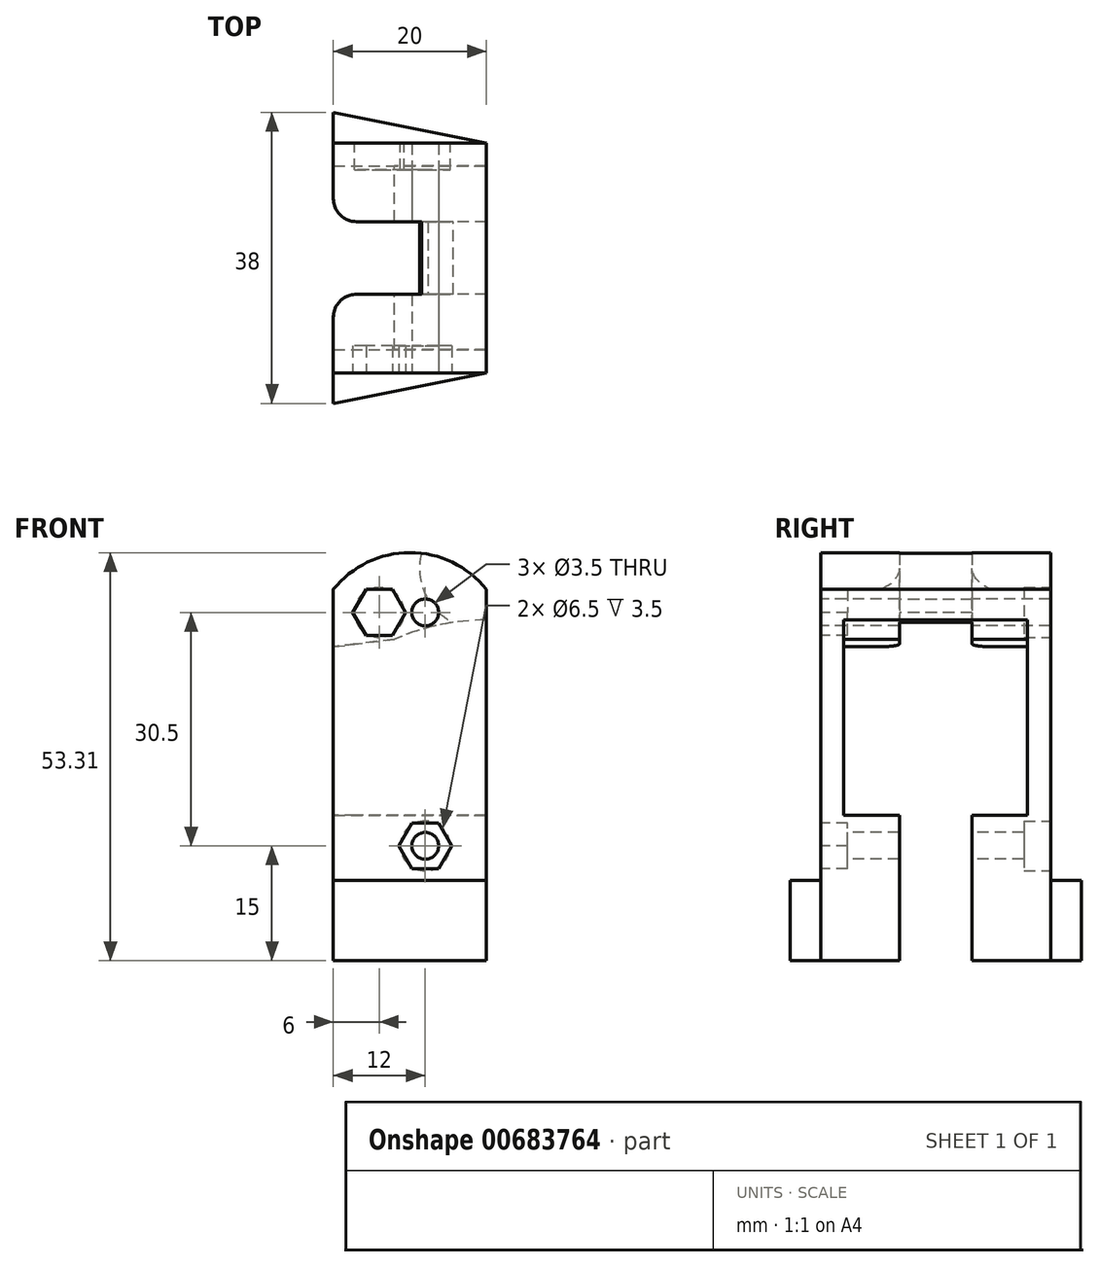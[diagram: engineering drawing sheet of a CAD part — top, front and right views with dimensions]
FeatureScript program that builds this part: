
annotation { "Feature Type Name" : "Feature", "Feature Type Description" : "" }
export const myFeature = defineFeature(function(context is Context, id is Id, definition is map)
    precondition{}
    {
        {
            var Q0;
            Q0=qCreatedBy(makeId("Front.planeOp"),FACE);
            var sketch = newSketch(context, id + "F0", { "sketchPlane" : qUnion([Q0])});
            skLineSegment(sketch, "E0", {"start": v(12, 0) * mm, "end": v(12, 38) * mm});
            skLineSegment(sketch, "E1", {"start": v(12, 0) * mm, "end": v(-8, 0) * mm});
            skLineSegment(sketch, "E2", {"start": v(-8, 0) * mm, "end": v(-8, 38) * mm});
            skArc(sketch, "E3", {"start": v(12, 38) * mm, "mid": v(2, 42.81) * mm, "end": v(-8, 38) * mm});
            skSolve(sketch);
        }
        {
            var Q0;
            Q0=qSketchRegion(id+"F0",true);
            extrude(context, id + "F1", {"entities" : qUnion([Q0]), "endBound" : BoundingType.SYMMETRIC, "depth" : 30 * mm, "offsetDistance" : 25 * mm});
        }
        {
            var Q0;
            Q0=qCreatedBy(makeId("Front.planeOp"),FACE);
            var sketch = newSketch(context, id + "F2", { "sketchPlane" : qUnion([Q0])});
            skLineSegment(sketch, "E4.bottom", {"start": v(12, 0) * mm, "end": v(-8, 0) * mm});
            skLineSegment(sketch, "E4.top", {"start": v(12, -10.5) * mm, "end": v(-8, -10.5) * mm});
            skLineSegment(sketch, "E4.left", {"start": v(12, 0) * mm, "end": v(12, -10.5) * mm});
            skLineSegment(sketch, "E4.right", {"start": v(-8, 0) * mm, "end": v(-8, -10.5) * mm});
            skSolve(sketch);
        }
        {
            var Q0;
            Q0 = qSketchRegion(id + "F2", true);
            extrude(context, id + "F3", {"entities" : qUnion([Q0]), "operationType" : NewBodyOperationType.ADD, "endBound" : BoundingType.SYMMETRIC, "depth" : 38 * mm, "offsetDistance" : 25 * mm});
        }
        {
            var Q0;
            Q0=qCreatedBy(makeId("Front.planeOp"),FACE);
            var sketch = newSketch(context, id + "F4", { "sketchPlane" : qUnion([Q0])});
            skLineSegment(sketch, "E5", {"start": v(12, 33) * mm, "end": v(12, 0) * mm});
            skLineSegment(sketch, "E6", {"start": v(12, 0) * mm, "end": v(-8, 0) * mm});
            skLineSegment(sketch, "E7", {"start": v(-8, 0) * mm, "end": v(-8, 44) * mm});
            skLineSegment(sketch, "E8", {"start": v(-8, 44) * mm, "end": v(4, 44) * mm});
            skArc(sketch, "E9", {"start": v(4, 44) * mm, "mid": v(4.74, 36.13) * mm, "end": v(12, 33) * mm});
            skLineSegment(sketch, "E10.bottom", {"start": v(-8, 0) * mm, "end": v(12, 0) * mm});
            skLineSegment(sketch, "E10.top", {"start": v(-8, -10.5) * mm, "end": v(12, -10.5) * mm});
            skLineSegment(sketch, "E10.left", {"start": v(-8, 0) * mm, "end": v(-8, -10.5) * mm});
            skLineSegment(sketch, "E10.right", {"start": v(12, 0) * mm, "end": v(12, -10.5) * mm});
            skSolve(sketch);
        }
        {
            var Q0;
            Q0=qSketchRegion(id+"F4",true);
            extrude(context, id + "F5", {"entities" : qUnion([Q0]), "endBound" : BoundingType.SYMMETRIC, "depth" : 9.5 * mm, "offsetDistance" : 25 * mm});
        }
        {
            var Q0;
            Q0=makeQuery(id+"F5.opExtrude","SWEPT_BODY",BODY,{"disambiguationData":[OSD([sQuery(id+"F4.wireOp",EDGE,"E5"),sQuery(id+"F4.wireOp",EDGE,"E6"),sQuery(id+"F4.wireOp",EDGE,"E7"),sQuery(id+"F4.wireOp",EDGE,"E8"),sQuery(id+"F4.wireOp",EDGE,"E9")])]});
            var Q1;
            Q1=makeQuery(id+"F1.opExtrude","SWEPT_BODY",BODY,{"disambiguationData":[OSD([sQuery(id+"F0.wireOp",EDGE,"E0"),sQuery(id+"F0.wireOp",EDGE,"E1"),sQuery(id+"F0.wireOp",EDGE,"E2"),sQuery(id+"F0.wireOp",EDGE,"wCZod6ud-FZbi-FoOU-Xc4i-ukdt4x6g0iyu")])]});
            booleanBodies(context, id + "F6", {"operationType" : BooleanOperationType.SUBTRACTION, "tools" : qUnion([Q0]), "targets" : qUnion([Q1])});
        }
        {
            var Q0;
            Q0=makeQuery(id+"F1.opExtrude","CAP_FACE",FACE,{"disambiguationData":[OSD([sQuery(id+"F0.wireOp",EDGE,"E0"),sQuery(id+"F0.wireOp",EDGE,"E1"),sQuery(id+"F0.wireOp",EDGE,"E2"),sQuery(id+"F0.wireOp",EDGE,"wCZod6ud-FZbi-FoOU-Xc4i-ukdt4x6g0iyu")])],"isStart":false});
            var sketch = newSketch(context, id + "F7", { "sketchPlane" : qUnion([Q0])});
            skLineSegment(sketch, "E11.bottom", {"start": v(-2, 4.5) * mm, "end": v(4, 4.5) * mm});
            skLineSegment(sketch, "E11.top", {"start": v(-2, 35) * mm, "end": v(4, 35) * mm});
            skLineSegment(sketch, "E11.left", {"start": v(4, 4.5) * mm, "end": v(4, 35) * mm});
            skLineSegment(sketch, "E11.right", {"start": v(-2, 4.5) * mm, "end": v(-2, 35) * mm});
            skSolve(sketch);
        }
        {
            var Q0;
            Q0=sQuery(id+"F7.wireOp",VERTEX,"E11.top.end");
            var Q1;
            Q1=sQuery(id+"F7.wireOp",VERTEX,"E11.left.start");
            var Q2;
            Q2=makeQuery(id+"F1.opExtrude","SWEPT_BODY",BODY,{"disambiguationData":[OSD([sQuery(id+"F0.wireOp",EDGE,"E0"),sQuery(id+"F0.wireOp",EDGE,"E1"),sQuery(id+"F0.wireOp",EDGE,"E2"),sQuery(id+"F0.wireOp",EDGE,"wCZod6ud-FZbi-FoOU-Xc4i-ukdt4x6g0iyu")])]});
            hole(context, id + "F8", {"style" : HoleStyle.SIMPLE, "endStyle" : HoleEndStyle.THROUGH, "holeDiameter" : 3.5 * mm, "majorDiameter" : 5 * mm, "tappedDepth" : 12 * mm, "tapClearance" : 3, "locations" : qUnion([Q0, Q1]), "scope" : qUnion([Q2])});
        }
        {
            var Q0;
            Q0=qCreatedBy(makeId("Front.planeOp"),FACE);
            var sketch = newSketch(context, id + "F9", { "sketchPlane" : qUnion([Q0])});
            skLineSegment(sketch, "E12.top", {"start": v(-8, 8.5) * mm, "end": v(12, 8.5) * mm});
            skLineSegment(sketch, "E12.left", {"start": v(-8, 30.5) * mm, "end": v(-8, 8.5) * mm});
            skLineSegment(sketch, "E12.right", {"start": v(12, 34) * mm, "end": v(12, 8.5) * mm});
            skLineSegment(sketch, "E13", {"start": v(-8, 30.5) * mm, "end": v(0, 31.5) * mm});
            skArc(sketch, "E14", {"start": v(12, 34) * mm, "mid": v(5.87, 33.37) * mm, "end": v(0, 31.5) * mm});
            skSolve(sketch);
        }
        {
            var Q0;
            Q0 = qSketchRegion(id + "F9", true);
            extrude(context, id + "F10", {"entities" : qUnion([Q0]), "operationType" : NewBodyOperationType.REMOVE, "endBound" : BoundingType.SYMMETRIC, "depth" : 24 * mm, "offsetDistance" : 25 * mm});
        }
        {
            var Q0;
            Q0=makeQuery(id+"F7.imprint","IMPRINT",FACE,{"disambiguationData":[TD([[makeQuery(id+"F7.imprint","IMPRINT",EDGE,{"derivedFrom":sQuery(id+"F7.wireOp",EDGE,"E11.bottom")}),-1.0]])]});
            var sketch = newSketch(context, id + "F11", { "sketchPlane" : qUnion([Q0])});
            skCircle(sketch, "E15.cCircle", {"center": v(-2, 35) * mm, "radius": 3 * mm, "construction": true});
            skLineSegment(sketch, "E15.0", {"start": v(1.46, 35) * mm, "end": v(-0.27, 32) * mm});
            skLineSegment(sketch, "E15.1", {"start": v(-0.27, 32) * mm, "end": v(-3.73, 32) * mm});
            skLineSegment(sketch, "E15.2", {"start": v(-3.73, 32) * mm, "end": v(-5.46, 35) * mm});
            skLineSegment(sketch, "E15.3", {"start": v(-5.46, 35) * mm, "end": v(-3.73, 38) * mm});
            skLineSegment(sketch, "E15.4", {"start": v(-3.73, 38) * mm, "end": v(-0.27, 38) * mm});
            skLineSegment(sketch, "E15.5", {"start": v(-0.27, 38) * mm, "end": v(1.46, 35) * mm});
            skPoint(sketch, "E15.0.midPoint", {"position": v(0.6, 33.5) * mm});
            skCircle(sketch, "E16.cCircle", {"center": v(4, 4.5) * mm, "radius": 3 * mm, "construction": true});
            skLineSegment(sketch, "E16.0", {"start": v(7.46, 4.5) * mm, "end": v(5.73, 1.5) * mm});
            skLineSegment(sketch, "E16.1", {"start": v(5.73, 1.5) * mm, "end": v(2.27, 1.5) * mm});
            skLineSegment(sketch, "E16.2", {"start": v(2.27, 1.5) * mm, "end": v(0.54, 4.5) * mm});
            skLineSegment(sketch, "E16.3", {"start": v(0.54, 4.5) * mm, "end": v(2.27, 7.5) * mm});
            skLineSegment(sketch, "E16.4", {"start": v(2.27, 7.5) * mm, "end": v(5.73, 7.5) * mm});
            skLineSegment(sketch, "E16.5", {"start": v(5.73, 7.5) * mm, "end": v(7.46, 4.5) * mm});
            skPoint(sketch, "E16.0.midPoint", {"position": v(6.6, 3) * mm});
            skSolve(sketch);
        }
        {
            var Q0;
            Q0 = qSketchRegion(id + "F11", true);
            extrude(context, id + "F12", {"entities" : qUnion([Q0]), "operationType" : NewBodyOperationType.REMOVE, "oppositeDirection" : true, "depth" : 3.5 * mm, "offsetDistance" : 25 * mm});
        }
        {
            var Q0;
            Q0=makeQuery(id+"F1.opExtrude","CAP_FACE",FACE,{"disambiguationData":[OSD([sQuery(id+"F0.wireOp",EDGE,"E0"),sQuery(id+"F0.wireOp",EDGE,"E1"),sQuery(id+"F0.wireOp",EDGE,"E2"),sQuery(id+"F0.wireOp",EDGE,"E3")])],"isStart":true});
            var sketch = newSketch(context, id + "F13", { "sketchPlane" : qUnion([Q0])});
            skCircle(sketch, "E17", {"center": v(2, 35) * mm, "radius": 3.25 * mm});
            skCircle(sketch, "E18", {"center": v(-4, 4.5) * mm, "radius": 3.25 * mm});
            skSolve(sketch);
        }
        {
            var Q0;
            Q0 = qSketchRegion(id + "F13", true);
            extrude(context, id + "F14", {"entities" : qUnion([Q0]), "operationType" : NewBodyOperationType.REMOVE, "oppositeDirection" : true, "depth" : 3.5 * mm, "offsetDistance" : 25 * mm});
        }
        {
            var Q0;
            {var subQ0=makeQuery(id+"F1.opExtrude","SWEPT_FACE",FACE,{"disambiguationData":[OSD([sQuery(id+"F0.wireOp",EDGE,"E2")])]});var subQ1=makeQuery(id+"F5.opExtrude","CAP_FACE",FACE,{"disambiguationData":[OSD([sQuery(id+"F4.wireOp",EDGE,"E5"),sQuery(id+"F4.wireOp",EDGE,"E7"),sQuery(id+"F4.wireOp",EDGE,"E8"),sQuery(id+"F4.wireOp",EDGE,"E9"),sQuery(id+"F4.wireOp",EDGE,"E10.top"),sQuery(id+"F4.wireOp",EDGE,"E10.left"),sQuery(id+"F4.wireOp",EDGE,"E10.right")])],"isStart":true});Q0=makeQuery(id+"F10.boolean.opBoolean","SPLIT",EDGE,{"disambiguationData":[TD([makeQuery(id+"F3.opExtrude","SWEPT_FACE",FACE,{"disambiguationData":[OSD([sQuery(id+"F2.wireOp",EDGE,"E4.right")])]})])],"derivedFrom":makeQuery(id+"F6.opBoolean","INTERSECT",EDGE,{"derivedFrom":[subQ0,subQ1]})});}
            var Q1;
            {var subQ0=makeQuery(id+"F1.opExtrude","SWEPT_FACE",FACE,{"disambiguationData":[OSD([sQuery(id+"F0.wireOp",EDGE,"E2")])]});var subQ1=makeQuery(id+"F5.opExtrude","CAP_FACE",FACE,{"disambiguationData":[OSD([sQuery(id+"F4.wireOp",EDGE,"E5"),sQuery(id+"F4.wireOp",EDGE,"E7"),sQuery(id+"F4.wireOp",EDGE,"E8"),sQuery(id+"F4.wireOp",EDGE,"E9"),sQuery(id+"F4.wireOp",EDGE,"E10.top"),sQuery(id+"F4.wireOp",EDGE,"E10.left"),sQuery(id+"F4.wireOp",EDGE,"E10.right")])],"isStart":false});Q1=makeQuery(id+"F10.boolean.opBoolean","SPLIT",EDGE,{"disambiguationData":[TD([makeQuery(id+"F3.opExtrude","SWEPT_FACE",FACE,{"disambiguationData":[OSD([sQuery(id+"F2.wireOp",EDGE,"E4.right")])]})])],"derivedFrom":makeQuery(id+"F6.opBoolean","INTERSECT",EDGE,{"derivedFrom":[subQ0,subQ1]})});}
            var Q2;
            Q2=makeQuery(id+"F6.opBoolean","COPY",EDGE,{"derivedFrom":makeQuery(id+"F5.opExtrude","CAP_EDGE",EDGE,{"disambiguationData":[OSD([sQuery(id+"F4.wireOp",EDGE,"E7"),sQuery(id+"F4.wireOp",EDGE,"E10.left")])],"isStart":true})});
            var Q3;
            Q3=makeQuery(id+"F6.opBoolean","COPY",EDGE,{"derivedFrom":makeQuery(id+"F5.opExtrude","CAP_EDGE",EDGE,{"disambiguationData":[OSD([sQuery(id+"F4.wireOp",EDGE,"E7"),sQuery(id+"F4.wireOp",EDGE,"E10.left")])],"isStart":false})});
            fillet(context, id + "F15", {"entities" : qUnion([Q0, Q1, Q2, Q3]), "radius" : 3 * mm, "tangentPropagation" : true, "allowEdgeOverflow" : false});
        }
        {
            var Q0;
            Q0=qCreatedBy(makeId("Top.planeOp"),FACE);
            var sketch = newSketch(context, id + "F16", { "sketchPlane" : qUnion([Q0])});
            skLineSegment(sketch, "E19", {"start": v(12, -15) * mm, "end": v(12, -19) * mm});
            skLineSegment(sketch, "E20", {"start": v(12, -19) * mm, "end": v(-8, -19) * mm});
            skLineSegment(sketch, "E21", {"start": v(-8, -19) * mm, "end": v(12, -15) * mm});
            skSolve(sketch);
        }
        {
            var Q0;
            Q0 = qSketchRegion(id + "F16", true);
            extrude(context, id + "F17", {"entities" : qUnion([Q0]), "oppositeDirection" : true, "depth" : 25 * mm, "offsetDistance" : 25 * mm});
        }
        {
            var Q0;
            Q0=makeQuery(id+"F17.opExtrude","SWEPT_BODY",BODY,{"disambiguationData":[OSD([sQuery(id+"F16.wireOp",EDGE,"E19"),sQuery(id+"F16.wireOp",EDGE,"E20"),sQuery(id+"F16.wireOp",EDGE,"E21")])]});
            var Q1;
            Q1=qCreatedBy(makeId("Front.planeOp"),FACE);
            mirror(context, id + "F18", {"entities" : qUnion([Q0]), "mirrorPlane" : qUnion([Q1])});
        }
        {
            var Q0;
            Q0=makeQuery(id+"F17.opExtrude","SWEPT_BODY",BODY,{"disambiguationData":[OSD([sQuery(id+"F16.wireOp",EDGE,"E19"),sQuery(id+"F16.wireOp",EDGE,"E20"),sQuery(id+"F16.wireOp",EDGE,"E21")])]});
            var Q1;
            Q1=makeQuery(id+"F18.opPattern","COPY",BODY,{"derivedFrom":makeQuery(id+"F17.opExtrude","SWEPT_BODY",BODY,{"disambiguationData":[OSD([sQuery(id+"F16.wireOp",EDGE,"E19"),sQuery(id+"F16.wireOp",EDGE,"E20"),sQuery(id+"F16.wireOp",EDGE,"E21")])]}),"instanceName":"1"});
            var Q2;
            Q2=makeQuery(id+"F1.opExtrude","SWEPT_BODY",BODY,{"disambiguationData":[OSD([sQuery(id+"F0.wireOp",EDGE,"E0"),sQuery(id+"F0.wireOp",EDGE,"E1"),sQuery(id+"F0.wireOp",EDGE,"E2"),sQuery(id+"F0.wireOp",EDGE,"E3")])]});
            booleanBodies(context, id + "F19", {"operationType" : BooleanOperationType.SUBTRACTION, "tools" : qUnion([Q0, Q1]), "targets" : qUnion([Q2])});
        }
    });
